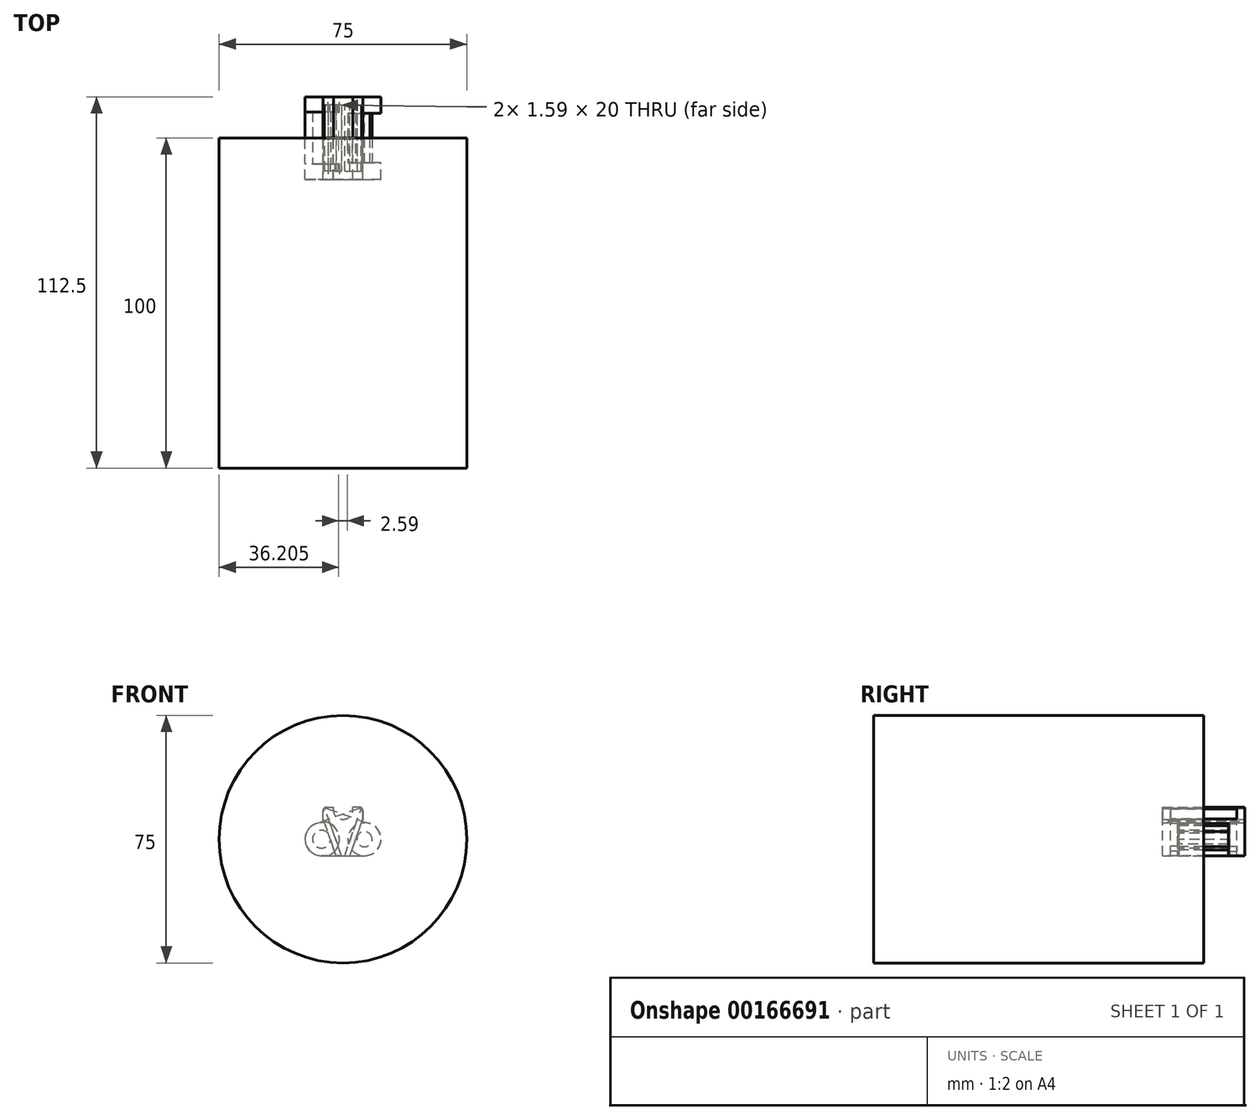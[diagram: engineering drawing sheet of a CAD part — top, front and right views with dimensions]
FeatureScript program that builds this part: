
annotation { "Feature Type Name" : "Feature", "Feature Type Description" : "" }
export const myFeature = defineFeature(function(context is Context, id is Id, definition is map)
    precondition{}
    {
        {
            assignVariable(context, id + "F0", {"name" : "length", "anyValue" : 25});
        }
        {
            assignVariable(context, id + "F1", {"name" : "joint", "anyValue" : 15});
        }
        {
            assignVariable(context, id + "F2", {"name" : "airgap", "anyValue" : 0.4});
        }
        {
            var Q0;
            Q0=qCreatedBy(makeId("Front.planeOp"),FACE);
            var sketch = newSketch(context, id + "F3", { "sketchPlane" : qUnion([Q0])});
            skCircle(sketch, "E0", {"center": v(-6.5, 0) * mm, "radius": 5 * mm});
            skCircle(sketch, "E1", {"center": v(6.5, 0) * mm, "radius": 5 * mm});
            skLineSegment(sketch, "E2", {"start": v(-6.5, -5) * mm, "end": v(6.5, -5) * mm});
            skLineSegment(sketch, "E3", {"start": v(-6.5, -5) * mm, "end": v(-6.5, 5) * mm});
            skLineSegment(sketch, "E4", {"start": v(-6.5, 5) * mm, "end": v(-6, 5) * mm});
            skLineSegment(sketch, "E5", {"start": v(-6, 5) * mm, "end": v(-6, 9.7) * mm});
            skLineSegment(sketch, "E6", {"start": v(6, 9.7) * mm, "end": v(6, 5) * mm});
            skLineSegment(sketch, "E7", {"start": v(6, 5) * mm, "end": v(6.5, 5) * mm});
            skLineSegment(sketch, "E8", {"start": v(6.5, 5) * mm, "end": v(6.5, -5) * mm});
            skLineSegment(sketch, "E9", {"start": v(-6, 9.7) * mm, "end": v(-2.92, 9.7) * mm});
            skLineSegment(sketch, "E10", {"start": v(6, 9.7) * mm, "end": v(2.92, 9.7) * mm});
            skArc(sketch, "E11", {"start": v(-2.92, 9.7) * mm, "mid": v(0, 6) * mm, "end": v(2.92, 9.7) * mm});
            skPoint(sketch, "E12", {"position": v(0, 6) * mm});
            skPoint(sketch, "E13", {"position": v(-1.5, 0) * mm});
            skPoint(sketch, "E14", {"position": v(1.5, 0) * mm});
            skSolve(sketch);
        }
        {
            var Q0;
            Q0=qSketchRegion(id+"F3",true);
            extrude(context, id + "F4", {"entities" : qUnion([Q0]), "depth" : (getVariable(context, 'length')) * mm, "symmetric" : true});
        }
        {
            var Q0;
            Q0=qCreatedBy(makeId("Front.planeOp"),FACE);
            var sketch = newSketch(context, id + "F5", { "sketchPlane" : qUnion([Q0])});
            skCircle(sketch, "E15", {"center": v(6.5, 0) * mm, "radius": 5 * mm});
            skCircle(sketch, "E16", {"center": v(6.5, 0) * mm, "radius": 2.3 * mm});
            skSolve(sketch);
        }
        {
            var Q0;
            Q0=qSketchRegion(id+"F5",true);
            extrude(context, id + "F6", {"entities" : qUnion([Q0]), "operationType" : NewBodyOperationType.REMOVE, "oppositeDirection" : true, "depth" : (getVariable(context, 'joint')) * mm, "symmetric" : true});
        }
        {
            var Q0;
            Q0=makeQuery(id+"F4.opExtrude","CAP_FACE",FACE,{"disambiguationData":[OSD([sQuery(id+"F3.wireOp",EDGE,"E0"),sQuery(id+"F3.wireOp",EDGE,"E1"),sQuery(id+"F3.wireOp",EDGE,"b1W5b6Qk-XJjz-mwui-rzEW-A7iv3fMp2VGR"),sQuery(id+"F3.wireOp",EDGE,"E2"),sQuery(id+"F3.wireOp",EDGE,"cOXluEr7-XomK-Si1W-8OtK-eNpiqizpjvTB"),sQuery(id+"F3.wireOp",EDGE,"Z6HJF1nQ-sOhT-L9r7-I5jc-SnCFn9Uo4Woa"),sQuery(id+"F3.wireOp",EDGE,"IznkMz8h-r0Hy-XQgO-IT0N-Dni7naP5gj2n"),sQuery(id+"F3.wireOp",EDGE,"Kvr3lOic-ohhp-PaTM-Kadp-Ef5VHRasuCZy")])],"isStart":false});
            var sketch = newSketch(context, id + "F7", { "sketchPlane" : qUnion([Q0])});
            skCircle(sketch, "E17", {"center": v(-6.5, 0) * mm, "radius": 5.4 * mm});
            skSolve(sketch);
        }
        {
            var Q0;
            Q0=qSketchRegion(id+"F7",true);
            extrude(context, id + "F8", {"entities" : qUnion([Q0]), "operationType" : NewBodyOperationType.REMOVE, "oppositeDirection" : true, "depth" : ((getVariable(context, 'length') - getVariable(context, 'joint') - 2 * getVariable(context, 'airgap')) / 2) * mm});
        }
        {
            var Q0;
            Q0=makeQuery(id+"F4.opExtrude","CAP_FACE",FACE,{"disambiguationData":[OSD([sQuery(id+"F3.wireOp",EDGE,"E0"),sQuery(id+"F3.wireOp",EDGE,"E1"),sQuery(id+"F3.wireOp",EDGE,"b1W5b6Qk-XJjz-mwui-rzEW-A7iv3fMp2VGR"),sQuery(id+"F3.wireOp",EDGE,"E2"),sQuery(id+"F3.wireOp",EDGE,"cOXluEr7-XomK-Si1W-8OtK-eNpiqizpjvTB"),sQuery(id+"F3.wireOp",EDGE,"Z6HJF1nQ-sOhT-L9r7-I5jc-SnCFn9Uo4Woa"),sQuery(id+"F3.wireOp",EDGE,"IznkMz8h-r0Hy-XQgO-IT0N-Dni7naP5gj2n"),sQuery(id+"F3.wireOp",EDGE,"Kvr3lOic-ohhp-PaTM-Kadp-Ef5VHRasuCZy")])],"isStart":true});
            var sketch = newSketch(context, id + "F9", { "sketchPlane" : qUnion([Q0])});
            skCircle(sketch, "E18", {"center": v(6.5, 0) * mm, "radius": 5.4 * mm});
            skSolve(sketch);
        }
        {
            var Q0;
            Q0=qSketchRegion(id+"F9",true);
            extrude(context, id + "F10", {"entities" : qUnion([Q0]), "operationType" : NewBodyOperationType.REMOVE, "oppositeDirection" : true, "depth" : ((getVariable(context, 'length') - getVariable(context, 'joint') - 2 * getVariable(context, 'airgap')) / 2) * mm});
        }
        {
            var Q0;
            Q0=makeQuery(id+"F4.opExtrude","CAP_FACE",FACE,{"disambiguationData":[OSD([sQuery(id+"F3.wireOp",EDGE,"E0"),sQuery(id+"F3.wireOp",EDGE,"E1"),sQuery(id+"F3.wireOp",EDGE,"b1W5b6Qk-XJjz-mwui-rzEW-A7iv3fMp2VGR"),sQuery(id+"F3.wireOp",EDGE,"E2"),sQuery(id+"F3.wireOp",EDGE,"cOXluEr7-XomK-Si1W-8OtK-eNpiqizpjvTB"),sQuery(id+"F3.wireOp",EDGE,"Z6HJF1nQ-sOhT-L9r7-I5jc-SnCFn9Uo4Woa"),sQuery(id+"F3.wireOp",EDGE,"IznkMz8h-r0Hy-XQgO-IT0N-Dni7naP5gj2n"),sQuery(id+"F3.wireOp",EDGE,"Kvr3lOic-ohhp-PaTM-Kadp-Ef5VHRasuCZy")])],"isStart":false});
            var sketch = newSketch(context, id + "F11", { "sketchPlane" : qUnion([Q0])});
            skCircle(sketch, "E19", {"center": v(-6.5, 0) * mm, "radius": 2.7 * mm});
            skSolve(sketch);
        }
        {
            var Q0;
            Q0=qSketchRegion(id+"F11",true);
            extrude(context, id + "F12", {"entities" : qUnion([Q0]), "operationType" : NewBodyOperationType.REMOVE, "endBound" : BoundingType.THROUGH_ALL, "oppositeDirection" : true, "depth" : 25 * mm});
        }
        {
            var Q0;
            Q0=qCreatedBy(makeId("Front.planeOp"),FACE);
            var sketch = newSketch(context, id + "F13", { "sketchPlane" : qUnion([Q0])});
            skCircle(sketch, "E20", {"center": v(-6.5, 0) * mm, "radius": 5 * mm});
            skCircle(sketch, "E21", {"center": v(6.5, 0) * mm, "radius": 5 * mm});
            skLineSegment(sketch, "E22.bottom", {"start": v(-6.5, 5) * mm, "end": v(6.5, 5) * mm});
            skLineSegment(sketch, "E22.top", {"start": v(-6.5, -5) * mm, "end": v(6.5, -5) * mm});
            skLineSegment(sketch, "E22.left", {"start": v(-6.5, 5) * mm, "end": v(-6.5, -5) * mm});
            skLineSegment(sketch, "E22.right", {"start": v(6.5, 5) * mm, "end": v(6.5, -5) * mm});
            skLineSegment(sketch, "E23", {"start": v(-6, 5) * mm, "end": v(-6, 9.7) * mm});
            skLineSegment(sketch, "E24", {"start": v(-6, 9.7) * mm, "end": v(8.16, 4.72) * mm});
            skSolve(sketch);
        }
        {
            var Q0;
            Q0 = qSketchRegion(id + "F13", true);
            extrude(context, id + "F14", {"entities" : qUnion([Q0]), "depth" : (getVariable(context, 'length')) * mm, "symmetric" : true});
        }
        {
            var Q0;
            Q0=makeQuery(id+"F14.opExtrude","CAP_FACE",FACE,{"disambiguationData":[OSD([sQuery(id+"F13.wireOp",EDGE,"E20"),sQuery(id+"F13.wireOp",EDGE,"E21"),sQuery(id+"F13.wireOp",EDGE,"E22.bottom"),sQuery(id+"F13.wireOp",EDGE,"E22.top"),sQuery(id+"F13.wireOp",EDGE,"E23"),sQuery(id+"F13.wireOp",EDGE,"E24")])],"isStart":false});
            var sketch = newSketch(context, id + "F15", { "sketchPlane" : qUnion([Q0])});
            skCircle(sketch, "E25", {"center": v(-6.5, 0) * mm, "radius": 5.4 * mm});
            skSolve(sketch);
        }
        {
            var Q0;
            Q0 = qSketchRegion(id + "F15", true);
            extrude(context, id + "F16", {"entities" : qUnion([Q0]), "operationType" : NewBodyOperationType.REMOVE, "oppositeDirection" : true, "depth" : (getVariable(context, 'length') - getVariable(context, 'joint') - 2 * getVariable(context, 'airgap')) / 2 * mm});
        }
        {
            var Q0;
            Q0=makeQuery(id+"F14.opExtrude","CAP_FACE",FACE,{"disambiguationData":[OSD([sQuery(id+"F13.wireOp",EDGE,"E20"),sQuery(id+"F13.wireOp",EDGE,"E21"),sQuery(id+"F13.wireOp",EDGE,"E22.bottom"),sQuery(id+"F13.wireOp",EDGE,"E22.top"),sQuery(id+"F13.wireOp",EDGE,"E23"),sQuery(id+"F13.wireOp",EDGE,"E24")])],"isStart":true});
            var sketch = newSketch(context, id + "F17", { "sketchPlane" : qUnion([Q0])});
            skCircle(sketch, "E26", {"center": v(6.5, 0) * mm, "radius": 5.4 * mm});
            skSolve(sketch);
        }
        {
            var Q0;
            Q0 = qSketchRegion(id + "F17", true);
            extrude(context, id + "F18", {"entities" : qUnion([Q0]), "operationType" : NewBodyOperationType.REMOVE, "oppositeDirection" : true, "depth" : ((getVariable(context, 'length') - getVariable(context, 'joint') - 2 * getVariable(context, 'airgap')) / 2) * mm});
        }
        {
            var Q0;
            Q0=qCreatedBy(makeId("Front.planeOp"),FACE);
            var sketch = newSketch(context, id + "F19", { "sketchPlane" : qUnion([Q0])});
            skCircle(sketch, "E27", {"center": v(-6.5, 0) * mm, "radius": 2.7 * mm});
            skSolve(sketch);
        }
        {
            var Q0;
            Q0 = qSketchRegion(id + "F19", true);
            extrude(context, id + "F20", {"entities" : qUnion([Q0]), "operationType" : NewBodyOperationType.REMOVE, "oppositeDirection" : true, "depth" : (getVariable(context, 'length')) * mm, "symmetric" : true});
        }
        {
            var Q0;
            Q0=qCreatedBy(makeId("Front.planeOp"),FACE);
            var sketch = newSketch(context, id + "F21", { "sketchPlane" : qUnion([Q0])});
            skCircle(sketch, "E28", {"center": v(-6.5, 0) * mm, "radius": 5 * mm});
            skCircle(sketch, "E29", {"center": v(6.5, 0) * mm, "radius": 5 * mm});
            skLineSegment(sketch, "E30.bottom", {"start": v(-6.5, 5) * mm, "end": v(6.5, 5) * mm});
            skLineSegment(sketch, "E30.top", {"start": v(-6.5, -5) * mm, "end": v(6.5, -5) * mm});
            skLineSegment(sketch, "E30.left", {"start": v(-6.5, 5) * mm, "end": v(-6.5, -5) * mm});
            skLineSegment(sketch, "E30.right", {"start": v(6.5, 5) * mm, "end": v(6.5, -5) * mm});
            skLineSegment(sketch, "E31", {"start": v(6, 5) * mm, "end": v(6, 9.7) * mm});
            skLineSegment(sketch, "E32", {"start": v(6, 9.7) * mm, "end": v(-8.16, 4.72) * mm});
            skSolve(sketch);
        }
        {
            var Q0;
            Q0 = qSketchRegion(id + "F21", true);
            extrude(context, id + "F22", {"entities" : qUnion([Q0]), "depth" : (getVariable(context, 'length')) * mm, "symmetric" : true});
        }
        {
            var Q0;
            Q0=qCreatedBy(makeId("Front.planeOp"),FACE);
            var sketch = newSketch(context, id + "F23", { "sketchPlane" : qUnion([Q0])});
            skCircle(sketch, "E33", {"center": v(6.5, 0) * mm, "radius": 5 * mm});
            skCircle(sketch, "E34", {"center": v(6.5, 0) * mm, "radius": 2.3 * mm});
            skSolve(sketch);
        }
        {
            var Q0;
            Q0 = qSketchRegion(id + "F23", true);
            extrude(context, id + "F24", {"entities" : qUnion([Q0]), "operationType" : NewBodyOperationType.REMOVE, "oppositeDirection" : true, "depth" : getVariable(context, 'joint') * mm, "symmetric" : true});
        }
        {
            var Q0;
            Q0=makeQuery(id+"F14.opExtrude","SWEPT_FACE",FACE,{"disambiguationData":[OSD([sQuery(id+"F13.wireOp",EDGE,"E24")])]});
            cPlane(context, id + "F25", {"entities" : qUnion([Q0]), "cplaneType" : CPlaneType.OFFSET, "offset" : 25 * mm, "width" : 150 * mm, "height" : 150 * mm});
        }
        {
            var Q0;
            Q0=qCreatedBy(id+"F25.planeOp",FACE);
            var sketch = newSketch(context, id + "F26", { "sketchPlane" : qUnion([Q0])});
            skLineSegment(sketch, "E35.bottom", {"start": v(2.13, -10) * mm, "end": v(3.63, -10) * mm});
            skLineSegment(sketch, "E35.top", {"start": v(2.13, 10) * mm, "end": v(3.63, 10) * mm});
            skLineSegment(sketch, "E35.left", {"start": v(2.13, -10) * mm, "end": v(2.13, 10) * mm});
            skLineSegment(sketch, "E35.right", {"start": v(3.63, -10) * mm, "end": v(3.63, 10) * mm});
            skSolve(sketch);
        }
        {
            var Q0;
            Q0 = qSketchRegion(id + "F26", true);
            extrude(context, id + "F27", {"entities" : qUnion([Q0]), "operationType" : NewBodyOperationType.REMOVE, "endBound" : BoundingType.THROUGH_ALL, "oppositeDirection" : true, "depth" : 25 * mm});
        }
        {
            var Q0;
            Q0=makeQuery(id+"F22.opExtrude","SWEPT_FACE",FACE,{"disambiguationData":[OSD([sQuery(id+"F21.wireOp",EDGE,"E32")])]});
            cPlane(context, id + "F28", {"entities" : qUnion([Q0]), "cplaneType" : CPlaneType.OFFSET, "offset" : 25 * mm, "width" : 150 * mm, "height" : 150 * mm});
        }
        {
            var Q0;
            Q0=qCreatedBy(id+"F28.planeOp",FACE);
            var sketch = newSketch(context, id + "F29", { "sketchPlane" : qUnion([Q0])});
            skLineSegment(sketch, "E36.top", {"start": v(-3.63, -10) * mm, "end": v(-2.13, -10) * mm});
            skLineSegment(sketch, "E36.left", {"start": v(-3.63, 10) * mm, "end": v(-3.63, -10) * mm});
            skLineSegment(sketch, "E36.right", {"start": v(-2.13, 10) * mm, "end": v(-2.13, -10) * mm});
            skLineSegment(sketch, "E37", {"start": v(-2.13, 10) * mm, "end": v(-3.63, 10) * mm});
            skSolve(sketch);
        }
        {
            var Q0;
            Q0 = qSketchRegion(id + "F29", true);
            extrude(context, id + "F30", {"entities" : qUnion([Q0]), "operationType" : NewBodyOperationType.REMOVE, "endBound" : BoundingType.THROUGH_ALL, "oppositeDirection" : true, "depth" : 25 * mm});
        }
        {
            var Q0;
            Q0=qCreatedBy(makeId("Front.planeOp"),FACE);
            var sketch = newSketch(context, id + "F31", { "sketchPlane" : qUnion([Q0])});
            skCircle(sketch, "E38", {"center": v(0, 0) * mm, "radius": 37.5 * mm});
            skSolve(sketch);
        }
        {
            var Q0;
            Q0 = qSketchRegion(id + "F31", true);
            extrude(context, id + "F32", {"entities" : qUnion([Q0]), "depth" : 100 * mm});
        }
        {
            var Q0;
            Q0=makeQuery(id+"F4.opExtrude","SWEPT_EDGE",EDGE,{"disambiguationData":[OSD([sQuery(id+"F3.wireOp",EDGE,"E5"),sQuery(id+"F3.wireOp",EDGE,"E9")])]});
            var Q1;
            Q1=makeQuery(id+"F4.opExtrude","SWEPT_EDGE",EDGE,{"disambiguationData":[OSD([sQuery(id+"F3.wireOp",EDGE,"E6"),sQuery(id+"F3.wireOp",EDGE,"E10")])]});
            var Q2;
            Q2=makeQuery(id+"F14.opExtrude","SWEPT_EDGE",EDGE,{"disambiguationData":[OSD([sQuery(id+"F13.wireOp",EDGE,"E23"),sQuery(id+"F13.wireOp",EDGE,"E24")])]});
            var Q3;
            Q3=makeQuery(id+"F22.opExtrude","SWEPT_EDGE",EDGE,{"disambiguationData":[OSD([sQuery(id+"F21.wireOp",EDGE,"E31"),sQuery(id+"F21.wireOp",EDGE,"E32")])]});
            fillet(context, id + "F33", {"entities" : qUnion([Q0, Q1, Q2, Q3]), "radius" : 1 * mm, "tangentPropagation" : true, "allowEdgeOverflow" : false});
        }
    });
